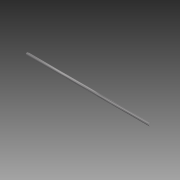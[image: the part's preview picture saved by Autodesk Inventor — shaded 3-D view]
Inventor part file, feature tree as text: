
AUTODESK INVENTOR PART (.ipt)
format: ipt  version: 2015 SP1 (Build 190203100, 203)  size: 83,968 bytes
history: native  units: in
note: dims shown in document units (in); Inventor stores cm internally (conversion verified against a paired STEP export)
features: extrude x1, sketch x1
ambient origin geometry x8: Origin, YZ Plane, XZ Plane, XY Plane, X Axis, Y Axis, Z Axis, Center Point
bodies: Solid1 (feature_tree)
feature tree (2):
  extrude  "Extrusion1"  Depth=23.0in TaperAngle=0.0deg
  sketch  "Sketch1"  dims[d0=0.375in d1=23.0in d2=0.0in]
